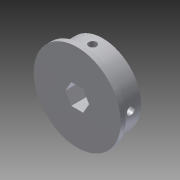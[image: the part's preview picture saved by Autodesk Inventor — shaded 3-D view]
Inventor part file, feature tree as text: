
AUTODESK INVENTOR PART (.ipt)
format: ipt  version: 2014 (Build 180170000, 170)  size: 159,744 bytes
history: native  units: in
note: dims shown in document units (in); Inventor stores cm internally (conversion verified against a paired STEP export)
features: extrude x6, sketch x6, plane x5, fillet x1, projected_geometry x1
ambient origin geometry x8: Origin, YZ Plane, XZ Plane, XY Plane, X Axis, Y Axis, Z Axis, Center Point
bodies: Solid1 (feature_tree)
feature tree (19):
  extrude  "Extrusion1"  Depth=0.502in
  plane  "Work Plane1"
  extrude  "Extrusion2"  Depth=0.5in
  plane  "Work Plane2"
  extrude  "Extrusion3"  Depth=0.2188in TaperAngle=0.0deg
  plane  "Work Plane4"
  extrude  "Extrusion4"  Depth=0.25in
  plane  "Work Plane5"
  extrude  "Extrusion5"  TaperAngle=150.0deg  [1 undecoded]
  extrude  "Extrusion6"  Depth=0.125in
  fillet  "Fillet1"  Radius=0.2188in
  sketch  "Sketch1"  dims[d0=1.873in d2=0.502in]
  sketch  "Sketch2"  dims[d3=0.5in d4=0.0in d5=0.19in]
  projected_geometry  "Projected Loop1"
  sketch  "Sketch3"  dims[d6=0.25in d7=0.2188in d8=0.0in]
  plane  "Work Plane3"
  sketch  "Sketch4"  dims[d9=0.19in d10=0.25in]
  sketch  "Sketch5"  dims[d11=0.2188in d12=0.0in d13=150.0deg]
  sketch  "Sketch6"  dims[d14=0.19in d15=0.25in d16=0.2188in d17=0.0in d18=0.19in d19=0.25in d20=0.2188in d21=0.0in d23=0.125in d24=0.0in d25=0.0312in d26=0.125in]
note: 1 required parameter value undecoded (feature->parameter linkage not recoverable at this tier; creation-order binding heuristic only, values carry confidence <= 0.55)
